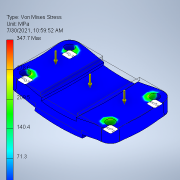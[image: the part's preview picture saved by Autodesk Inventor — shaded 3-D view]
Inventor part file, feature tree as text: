
AUTODESK INVENTOR PART (.ipt)
format: ipt  version: 2020 (Build 240168000, 168)  size: 199,680 bytes
history: native  units: mm
features: extrude x3, sketch x2, fillet x2, mirror x1
ambient origin geometry x8: Origin, YZ Plane, XZ Plane, XY Plane, X Axis, Y Axis, Z Axis, Center Point
bodies: Solid1 (feature_tree)
feature tree (8):
  extrude  "Extrusion1"  Depth=4.0mm
  sketch  "Sketch2"  dims[d2=38.0mm d3=16.0mm d4=44.0mm d5=4.0mm d6=82.0mm d7=0.0mm d8=11.0mm d9=11.0mm d10=12.0mm d11=12.0mm d12=12.0mm d13=12.0mm d14=82.0mm d15=0.0mm d16=82.0mm d17=0.0mm d18=12.0mm d19=12.0mm]
  extrude  "Extrusion2"  Depth=16.0mm
  extrude  "Extrusion3"  Depth=44.0mm
  fillet  "Fillet1"  Radius=4.0mm
  fillet  "Fillet2"  Radius=82.0mm
  mirror  "Mirror1"
  sketch  "Sketch1"  dims[d0=30.0mm d1=4.0mm]
